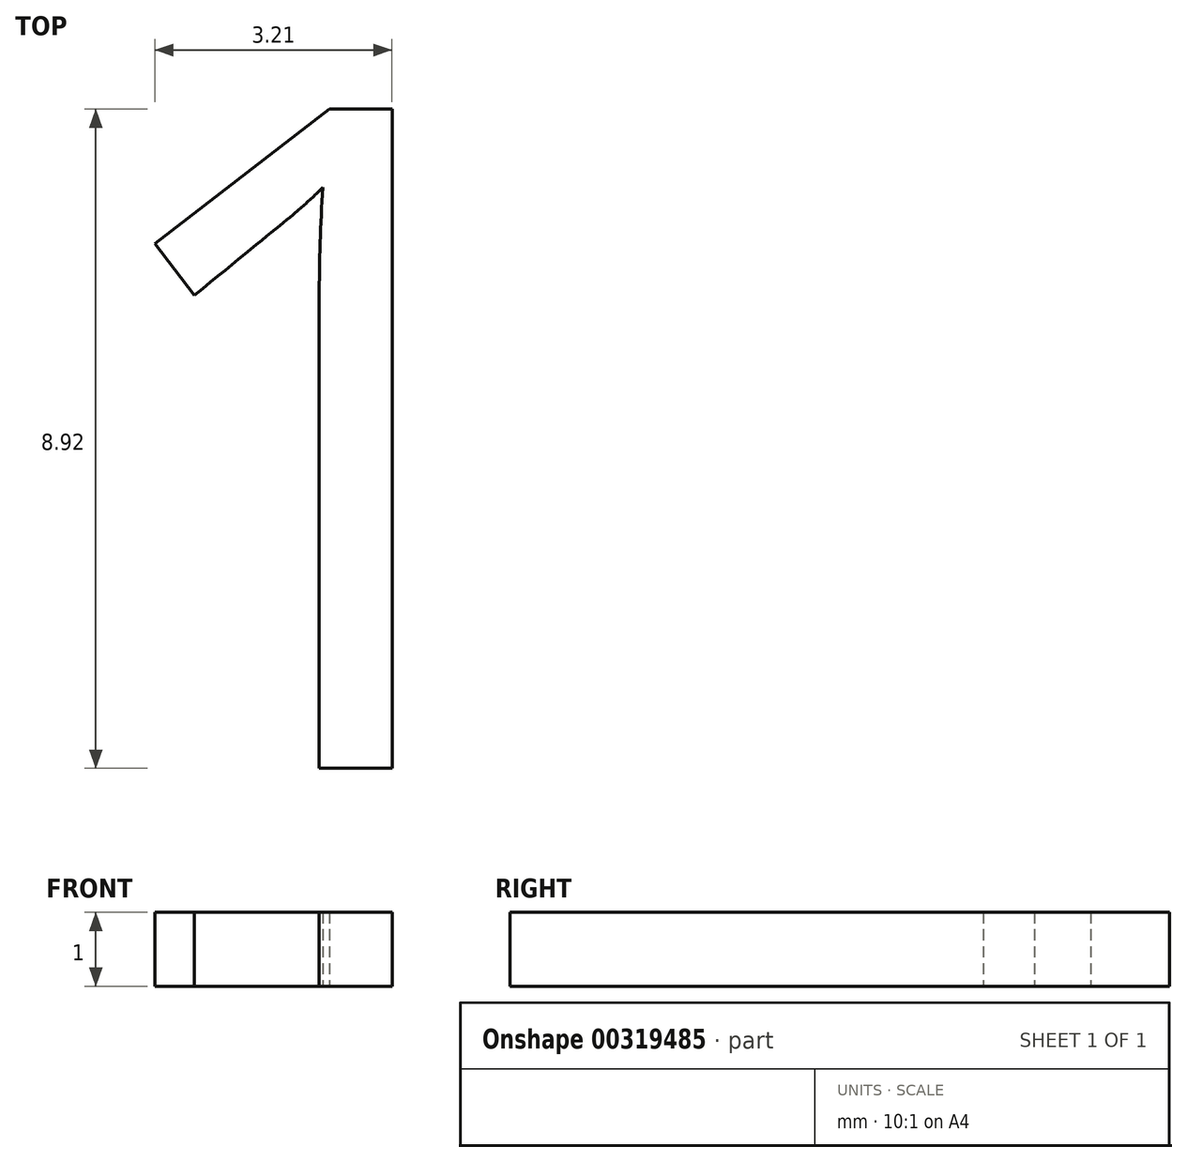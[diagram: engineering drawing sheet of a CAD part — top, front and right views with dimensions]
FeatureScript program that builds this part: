
annotation { "Feature Type Name" : "Feature", "Feature Type Description" : "" }
export const myFeature = defineFeature(function(context is Context, id is Id, definition is map)
    precondition{}
    {
        {
            var Q0;
            Q0=qCreatedBy(makeId("Top.planeOp"),FACE);
            var sketch = newSketch(context, id + "F0", { "sketchPlane" : qUnion([Q0])});
            skText(sketch, "E0", { "text": "1", "fontName": "OpenSans-Regular.ttf"});
            skText(sketch, "E1", { "text": "2", "fontName": "OpenSans-Bold.ttf"});
            skLineSegment(sketch, "E2.bottom", {"start": v(-81.57, -59.86) * mm, "end": v(-24.07, -59.86) * mm});
            skLineSegment(sketch, "E2.top", {"start": v(-81.57, -62.86) * mm, "end": v(-24.07, -62.86) * mm});
            skLineSegment(sketch, "E2.left", {"start": v(-81.57, -59.86) * mm, "end": v(-81.57, -62.86) * mm});
            skLineSegment(sketch, "E2.right", {"start": v(-24.07, -59.86) * mm, "end": v(-24.07, -62.86) * mm});
            skLineSegment(sketch, "E3.bottom", {"start": v(-8.57, -56.36) * mm, "end": v(23.43, -56.36) * mm});
            skLineSegment(sketch, "E3.top", {"start": v(-8.57, -66.36) * mm, "end": v(23.43, -66.36) * mm});
            skLineSegment(sketch, "E3.left", {"start": v(-8.57, -56.36) * mm, "end": v(-8.57, -66.36) * mm});
            skLineSegment(sketch, "E3.right", {"start": v(23.43, -56.36) * mm, "end": v(23.43, -66.36) * mm});
            skText(sketch, "E4", { "text": "1", "fontName": "OpenSans-Bold.ttf"});
            skLineSegment(sketch, "E5.bottom", {"start": v(-81.6, -44.86) * mm, "end": v(-24.1, -44.86) * mm});
            skLineSegment(sketch, "E5.top", {"start": v(-81.6, -47.86) * mm, "end": v(-24.1, -47.86) * mm});
            skLineSegment(sketch, "E5.left", {"start": v(-81.6, -44.86) * mm, "end": v(-81.6, -47.86) * mm});
            skLineSegment(sketch, "E5.right", {"start": v(-24.1, -44.86) * mm, "end": v(-24.1, -47.86) * mm});
            skLineSegment(sketch, "E6.bottom", {"start": v(-8.5, -41.36) * mm, "end": v(23.5, -41.36) * mm});
            skLineSegment(sketch, "E6.top", {"start": v(-8.5, -51.36) * mm, "end": v(23.5, -51.36) * mm});
            skLineSegment(sketch, "E6.left", {"start": v(-8.5, -41.36) * mm, "end": v(-8.5, -51.36) * mm});
            skLineSegment(sketch, "E6.right", {"start": v(23.5, -41.36) * mm, "end": v(23.5, -51.36) * mm});
            skLineSegment(sketch, "E7.left", {"start": v(-8.73, 3.64) * mm, "end": v(-8.73, -6.36) * mm});
            skLineSegment(sketch, "E8.left", {"start": v(-8.96, 78.64) * mm, "end": v(-8.96, 68.64) * mm});
            skLineSegment(sketch, "E9.bottom", {"start": v(-81.39, -29.86) * mm, "end": v(-23.89, -29.86) * mm});
            skLineSegment(sketch, "E9.top", {"start": v(-81.39, -32.86) * mm, "end": v(-23.89, -32.86) * mm});
            skLineSegment(sketch, "E9.left", {"start": v(-81.39, -29.86) * mm, "end": v(-81.39, -32.86) * mm});
            skLineSegment(sketch, "E9.right", {"start": v(-23.89, -29.86) * mm, "end": v(-23.89, -32.86) * mm});
            skLineSegment(sketch, "E10.bottom", {"start": v(-81.57, -14.86) * mm, "end": v(-24.07, -14.86) * mm});
            skLineSegment(sketch, "E10.top", {"start": v(-81.57, -17.86) * mm, "end": v(-24.07, -17.86) * mm});
            skLineSegment(sketch, "E10.left", {"start": v(-81.57, -14.86) * mm, "end": v(-81.57, -17.86) * mm});
            skLineSegment(sketch, "E10.right", {"start": v(-24.07, -14.86) * mm, "end": v(-24.07, -17.86) * mm});
            skLineSegment(sketch, "E11.bottom", {"start": v(-81.57, 0.14) * mm, "end": v(-24.07, 0.14) * mm});
            skLineSegment(sketch, "E11.top", {"start": v(-81.57, -2.86) * mm, "end": v(-24.07, -2.86) * mm});
            skLineSegment(sketch, "E11.left", {"start": v(-81.57, 0.14) * mm, "end": v(-81.57, -2.86) * mm});
            skLineSegment(sketch, "E11.right", {"start": v(-24.07, 0.14) * mm, "end": v(-24.07, -2.86) * mm});
            skLineSegment(sketch, "E12.bottom", {"start": v(-81.57, 15.14) * mm, "end": v(-24.07, 15.14) * mm});
            skLineSegment(sketch, "E12.top", {"start": v(-81.57, 12.14) * mm, "end": v(-24.07, 12.14) * mm});
            skLineSegment(sketch, "E12.left", {"start": v(-81.57, 15.14) * mm, "end": v(-81.57, 12.14) * mm});
            skLineSegment(sketch, "E12.right", {"start": v(-24.07, 15.14) * mm, "end": v(-24.07, 12.14) * mm});
            skLineSegment(sketch, "E13.bottom", {"start": v(-81.57, 30.14) * mm, "end": v(-24.07, 30.14) * mm});
            skLineSegment(sketch, "E13.top", {"start": v(-81.57, 27.14) * mm, "end": v(-24.07, 27.14) * mm});
            skLineSegment(sketch, "E13.left", {"start": v(-81.57, 30.14) * mm, "end": v(-81.57, 27.14) * mm});
            skLineSegment(sketch, "E13.right", {"start": v(-24.07, 30.14) * mm, "end": v(-24.07, 27.14) * mm});
            skLineSegment(sketch, "E14.bottom", {"start": v(-81.57, 45.14) * mm, "end": v(-24.07, 45.14) * mm});
            skLineSegment(sketch, "E14.top", {"start": v(-81.57, 42.14) * mm, "end": v(-24.07, 42.14) * mm});
            skLineSegment(sketch, "E14.left", {"start": v(-81.57, 45.14) * mm, "end": v(-81.57, 42.14) * mm});
            skLineSegment(sketch, "E14.right", {"start": v(-24.07, 45.14) * mm, "end": v(-24.07, 42.14) * mm});
            skLineSegment(sketch, "E15.bottom", {"start": v(-81.57, 60.14) * mm, "end": v(-24.07, 60.14) * mm});
            skLineSegment(sketch, "E15.top", {"start": v(-81.57, 57.14) * mm, "end": v(-24.07, 57.14) * mm});
            skLineSegment(sketch, "E15.left", {"start": v(-81.57, 60.14) * mm, "end": v(-81.57, 57.14) * mm});
            skLineSegment(sketch, "E15.right", {"start": v(-24.07, 60.14) * mm, "end": v(-24.07, 57.14) * mm});
            skLineSegment(sketch, "E16.bottom", {"start": v(-81.57, 75.14) * mm, "end": v(-24.07, 75.14) * mm});
            skLineSegment(sketch, "E16.top", {"start": v(-81.57, 72.14) * mm, "end": v(-24.07, 72.14) * mm});
            skLineSegment(sketch, "E16.left", {"start": v(-81.57, 75.14) * mm, "end": v(-81.57, 72.14) * mm});
            skLineSegment(sketch, "E16.right", {"start": v(-24.07, 75.14) * mm, "end": v(-24.07, 72.14) * mm});
            skText(sketch, "E17", { "text": "2", "fontName": "OpenSans-Bold.ttf"});
            skText(sketch, "E18", { "text": "3", "fontName": "OpenSans-Bold.ttf"});
            skText(sketch, "E19", { "text": "4", "fontName": "OpenSans-Bold.ttf"});
            skText(sketch, "E20", { "text": "5", "fontName": "OpenSans-Bold.ttf"});
            skText(sketch, "E21", { "text": "6", "fontName": "OpenSans-Bold.ttf"});
            skText(sketch, "E22", { "text": "7", "fontName": "OpenSans-Bold.ttf"});
            skText(sketch, "E23", { "text": "8", "fontName": "OpenSans-Bold.ttf"});
            skText(sketch, "E24", { "text": "9", "fontName": "OpenSans-Bold.ttf"});
            skText(sketch, "E25", { "text": "10", "fontName": "OpenSans-Regular.ttf"});
            const initialGuessF0  = {"E0": [-0.03558, 0.01785, 1, 0, 0.009], "E1": [-0.03815, 0.00452, 1, 0, 0.00974], "E4": [-0.01941, -0.06631, 1, 0, 0.01], "E17": [-0.01974, -0.05154, 1, 0, 0.01], "E18": [-0.0196, -0.03645, 1, 0, 0.01], "E19": [-0.0197, -0.02144, 1, 0, 0.01], "E20": [-0.01953, -0.00642, 1, 0, 0.01], "E21": [-0.0198, 0.0085, 1, 0, 0.01], "E22": [-0.02009, 0.02349, 1, 0, 0.01], "E23": [-0.02025, 0.03858, 1, 0, 0.01], "E24": [-0.0204, 0.05361, 1, 0, 0.01], "E25": [-0.02252, 0.06973, 1, 0, 0.008]};
            skSetInitialGuess(sketch, initialGuessF0);
            skSolve(sketch);
        }
        {
            var Q0;
            Q0=makeQuery(id+"F0.imprint","IMPRINT",FACE,{"disambiguationData":[TD([[makeQuery(id+"F0.imprint","IMPRINT",EDGE,{"derivedFrom":sQuery(id+"F0.wireOp",EDGE,"E0.sketch_text.stroke-0")}),-1.0]])]});
            extrude(context, id + "F1", {"entities" : qUnion([Q0]), "depth" : 1 * mm});
        }
    });
